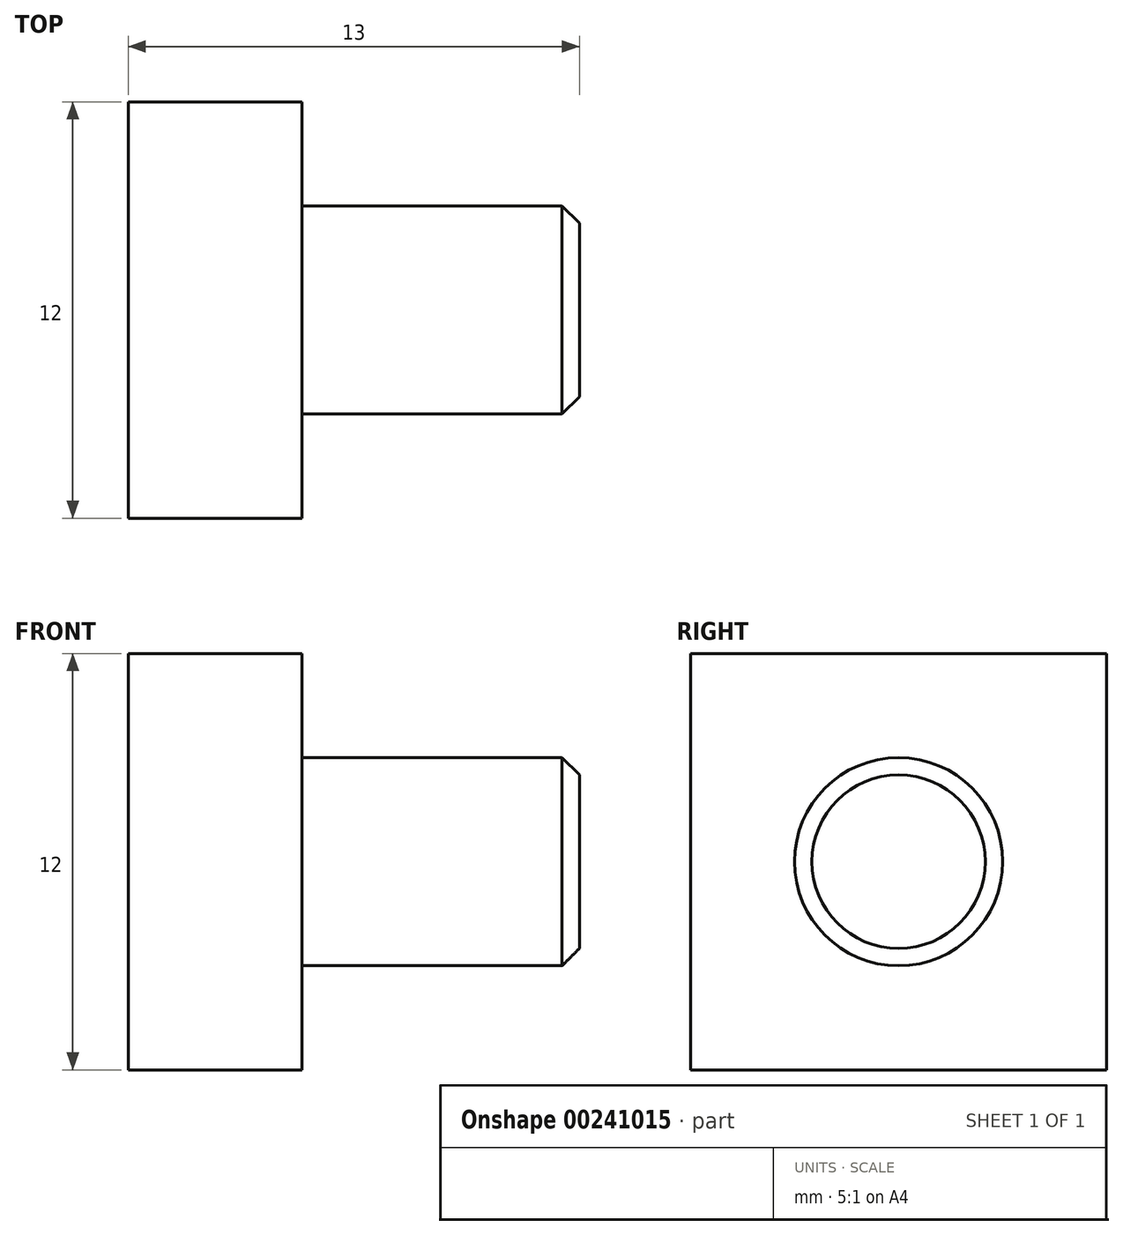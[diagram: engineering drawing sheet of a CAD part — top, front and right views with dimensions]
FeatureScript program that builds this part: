
annotation { "Feature Type Name" : "Feature", "Feature Type Description" : "" }
export const myFeature = defineFeature(function(context is Context, id is Id, definition is map)
    precondition{}
    {
        {
            var Q0;
            Q0=qCreatedBy(makeId("Right.planeOp"),FACE);
            var sketch = newSketch(context, id + "F0", { "sketchPlane" : qUnion([Q0])});
            skLineSegment(sketch, "E0.bottom", {"start": v(6, 6) * mm, "end": v(-6, 6) * mm});
            skLineSegment(sketch, "E0.top", {"start": v(6, -6) * mm, "end": v(-6, -6) * mm});
            skLineSegment(sketch, "E0.left", {"start": v(6, 6) * mm, "end": v(6, -6) * mm});
            skLineSegment(sketch, "E0.right", {"start": v(-6, 6) * mm, "end": v(-6, -6) * mm});
            skPoint(sketch, "E0.middle", {"position": v(0, 0) * mm});
            skSolve(sketch);
        }
        {
            var Q0;
            Q0 = qSketchRegion(id + "F0", true);
            extrude(context, id + "F1", {"entities" : qUnion([Q0]), "depth" : 5 * mm});
        }
        {
            var Q0;
            Q0=makeQuery(id+"F1.opExtrude","CAP_FACE",FACE,{"disambiguationData":[OSD([sQuery(id+"F0.wireOp",EDGE,"E0.bottom"),sQuery(id+"F0.wireOp",EDGE,"E0.top"),sQuery(id+"F0.wireOp",EDGE,"E0.left"),sQuery(id+"F0.wireOp",EDGE,"E0.right")])],"isStart":false});
            var sketch = newSketch(context, id + "F2", { "sketchPlane" : qUnion([Q0])});
            skCircle(sketch, "E1", {"center": v(0, 0) * mm, "radius": 3 * mm});
            skSolve(sketch);
        }
        {
            var Q0;
            Q0=makeQuery(id+"F2.imprint","IMPRINT",FACE,{"disambiguationData":[TD([[makeQuery(id+"F2.imprint","IMPRINT",EDGE,{"derivedFrom":sQuery(id+"F2.wireOp",EDGE,"E1")}),1.0]])]});
            extrude(context, id + "F3", {"entities" : qUnion([Q0]), "operationType" : NewBodyOperationType.ADD, "depth" : 8 * mm});
        }
        {
            var Q0;
            Q0=makeQuery(id+"F3.opExtrude","CAP_EDGE",EDGE,{"disambiguationData":[OSD([sQuery(id+"F2.wireOp",EDGE,"E1")])],"isStart":false});
            chamfer(context, id + "F4", {"entities" : qUnion([Q0]), "width" : 0.5 * mm, "tangentPropagation" : true});
        }
    });
